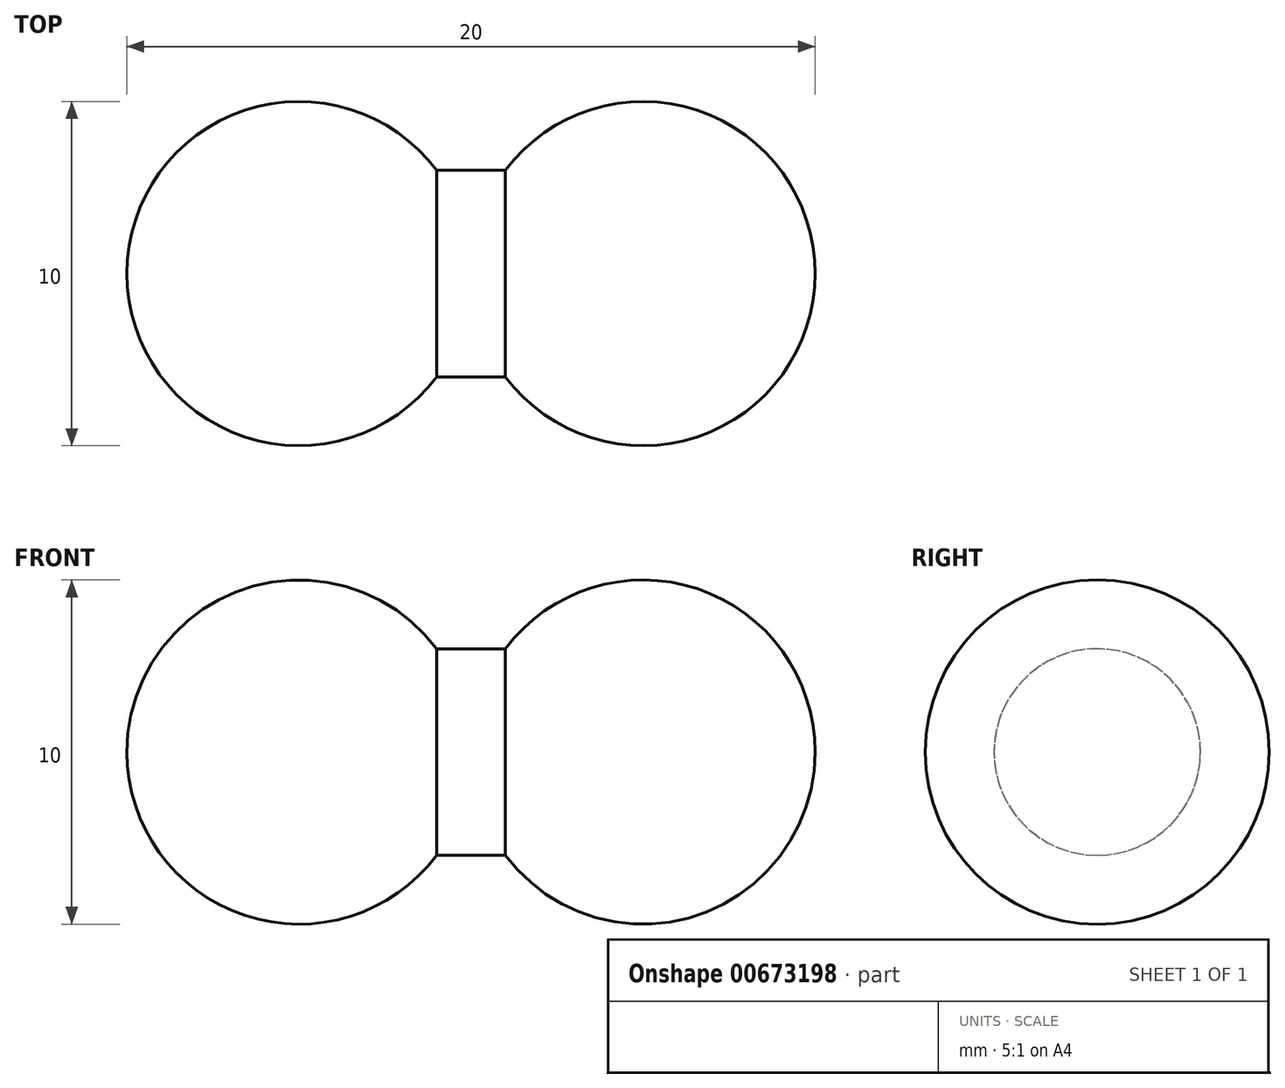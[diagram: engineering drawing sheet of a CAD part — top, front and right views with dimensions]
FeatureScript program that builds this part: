
annotation { "Feature Type Name" : "Feature", "Feature Type Description" : "" }
export const myFeature = defineFeature(function(context is Context, id is Id, definition is map)
    precondition{}
    {
        {
            var Q0;
            Q0=qCreatedBy(makeId("Front.planeOp"),FACE);
            var sketch = newSketch(context, id + "F0", { "sketchPlane" : qUnion([Q0])});
            skArc(sketch, "E0", {"start": v(17, 0) * mm, "mid": v(13.58, 4.74) * mm, "end": v(8, 3) * mm});
            skLineSegment(sketch, "E1", {"start": v(7, 0) * mm, "end": v(7, 3) * mm, "construction": true});
            skLineSegment(sketch, "E2", {"start": v(8, 3) * mm, "end": v(7, 3) * mm});
            skArc(sketch, "E3.MirrorCS", {"start": v(-3, 0) * mm, "mid": v(0.42, 4.74) * mm, "end": v(6, 3) * mm});
            skLineSegment(sketch, "E4", {"start": v(7, 3) * mm, "end": v(6, 3) * mm});
            skLineSegment(sketch, "E5", {"start": v(-3, 0) * mm, "end": v(17, 0) * mm});
            skPoint(sketch, "E6.orphan", {"position": v(7, 0) * mm});
            skSolve(sketch);
        }
        {
            var Q0;
            Q0=makeQuery(id+"F0.imprint","IMPRINT",FACE,{"disambiguationData":[TD([[makeQuery(id+"F0.imprint","IMPRINT",EDGE,{"derivedFrom":sQuery(id+"F0.wireOp",EDGE,"E0")}),1.0]])]});
            var Q1;
            Q1=sQuery(id+"F0.wireOp",EDGE,"E5");
            revolve(context, id + "F1", {"entities" : qUnion([Q0]), "axis" : qUnion([Q1]), "revolveType" : RevolveType.FULL});
        }
    });
